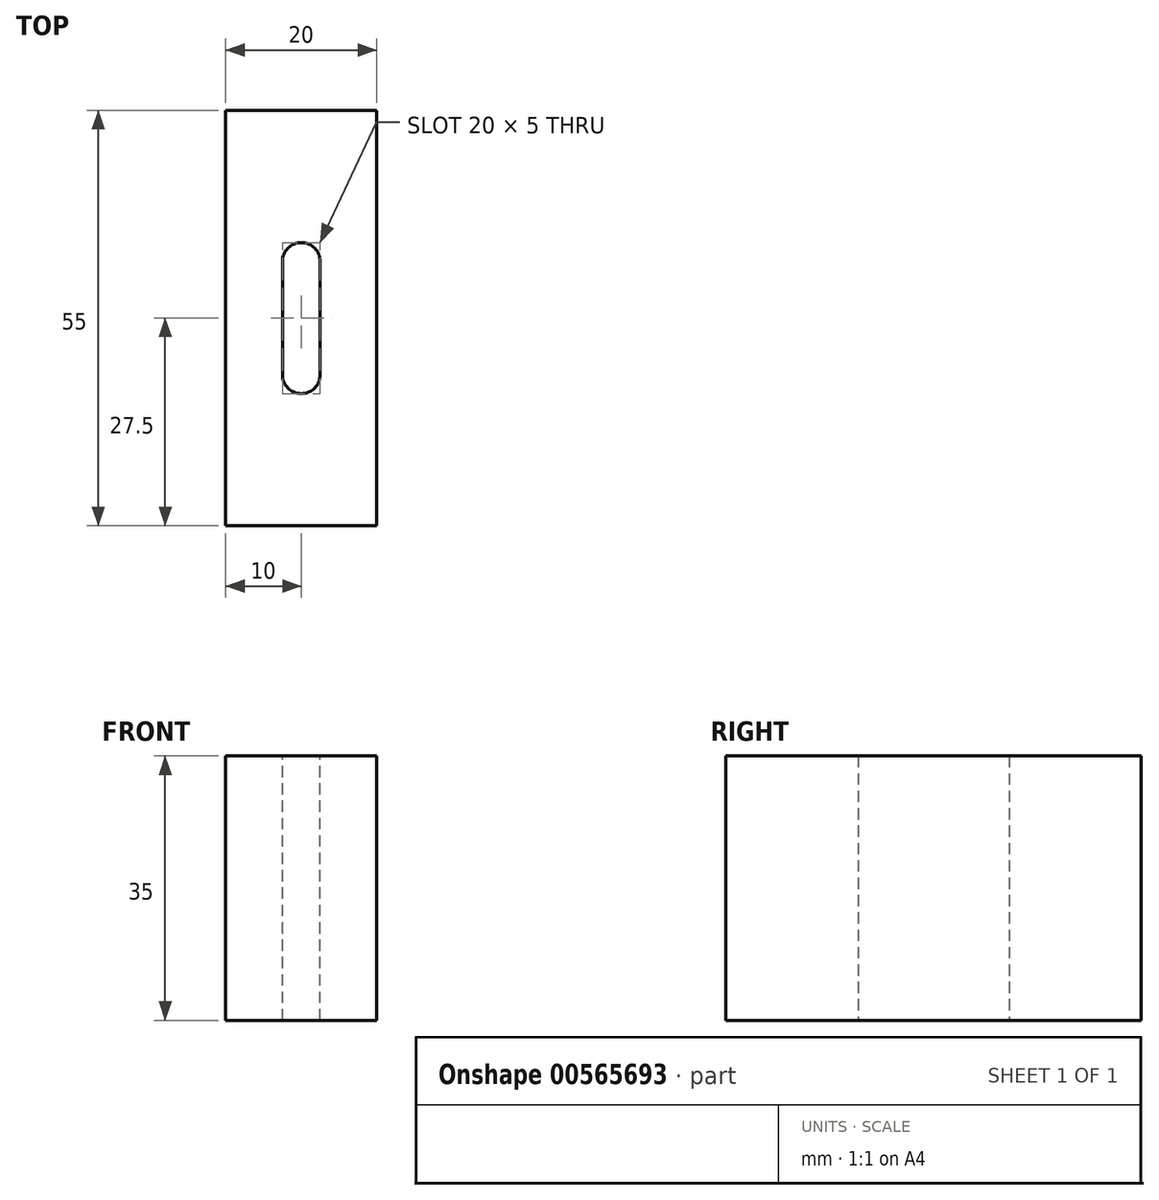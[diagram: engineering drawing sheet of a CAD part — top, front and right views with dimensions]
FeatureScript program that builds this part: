
annotation { "Feature Type Name" : "Feature", "Feature Type Description" : "" }
export const myFeature = defineFeature(function(context is Context, id is Id, definition is map)
    precondition{}
    {
        {
            var Q0;
            Q0=qCreatedBy(makeId("Top.planeOp"),FACE);
            var sketch = newSketch(context, id + "F0", { "sketchPlane" : qUnion([Q0])});
            skLineSegment(sketch, "E0.bottom", {"start": v(-10, -27.5) * mm, "end": v(10, -27.5) * mm});
            skLineSegment(sketch, "E0.top", {"start": v(-10, 27.5) * mm, "end": v(10, 27.5) * mm});
            skLineSegment(sketch, "E0.left", {"start": v(-10, -27.5) * mm, "end": v(-10, 27.5) * mm});
            skLineSegment(sketch, "E0.right", {"start": v(10, -27.5) * mm, "end": v(10, 27.5) * mm});
            skPoint(sketch, "E0.middle", {"position": v(0, 0) * mm});
            skSolve(sketch);
        }
        {
            var Q0;
            Q0 = qSketchRegion(id + "F0", true);
            extrude(context, id + "F1", {"entities" : qUnion([Q0]), "depth" : 35 * mm, "offsetDistance" : 25 * mm});
        }
        {
            var Q0;
            Q0=makeQuery(id+"F1.opExtrude","CAP_FACE",FACE,{"disambiguationData":[OSD([sQuery(id+"F0.wireOp",EDGE,"E0.bottom"),sQuery(id+"F0.wireOp",EDGE,"E0.top"),sQuery(id+"F0.wireOp",EDGE,"E0.left"),sQuery(id+"F0.wireOp",EDGE,"E0.right")])],"isStart":false});
            var sketch = newSketch(context, id + "F2", { "sketchPlane" : qUnion([Q0])});
            skLineSegment(sketch, "E1.bottom", {"start": v(-2.5, -10) * mm, "end": v(2.5, -10) * mm});
            skLineSegment(sketch, "E1.top", {"start": v(-2.5, 10) * mm, "end": v(2.5, 10) * mm});
            skLineSegment(sketch, "E1.left", {"start": v(-2.5, -10) * mm, "end": v(-2.5, 10) * mm});
            skLineSegment(sketch, "E1.right", {"start": v(2.5, -10) * mm, "end": v(2.5, 10) * mm});
            skPoint(sketch, "E1.middle", {"position": v(0, 0) * mm});
            skSolve(sketch);
        }
        {
            var Q0;
            Q0 = qSketchRegion(id + "F2", true);
            extrude(context, id + "F3", {"entities" : qUnion([Q0]), "operationType" : NewBodyOperationType.REMOVE, "endBound" : BoundingType.THROUGH_ALL, "oppositeDirection" : true, "depth" : 25 * mm, "offsetDistance" : 25 * mm});
        }
        {
            var Q0;
            Q0=makeQuery(id+"F3.boolean.opBoolean","COPY",EDGE,{"derivedFrom":makeQuery(id+"F3.opExtrude","SWEPT_EDGE",EDGE,{"disambiguationData":[OSD([sQuery(id+"F2.wireOp",EDGE,"E1.top"),sQuery(id+"F2.wireOp",EDGE,"E1.left")])]})});
            var Q1;
            Q1=makeQuery(id+"F3.boolean.opBoolean","COPY",EDGE,{"derivedFrom":makeQuery(id+"F3.opExtrude","SWEPT_EDGE",EDGE,{"disambiguationData":[OSD([sQuery(id+"F2.wireOp",EDGE,"E1.top"),sQuery(id+"F2.wireOp",EDGE,"E1.right")])]})});
            var Q2;
            Q2=makeQuery(id+"F3.boolean.opBoolean","COPY",EDGE,{"derivedFrom":makeQuery(id+"F3.opExtrude","SWEPT_EDGE",EDGE,{"disambiguationData":[OSD([sQuery(id+"F2.wireOp",EDGE,"E1.bottom"),sQuery(id+"F2.wireOp",EDGE,"E1.right")])]})});
            var Q3;
            Q3=makeQuery(id+"F3.boolean.opBoolean","COPY",EDGE,{"derivedFrom":makeQuery(id+"F3.opExtrude","SWEPT_EDGE",EDGE,{"disambiguationData":[OSD([sQuery(id+"F2.wireOp",EDGE,"E1.bottom"),sQuery(id+"F2.wireOp",EDGE,"E1.left")])]})});
            fillet(context, id + "F4", {"entities" : qUnion([Q0, Q1, Q2, Q3]), "radius" : 2.5 * mm, "tangentPropagation" : true, "allowEdgeOverflow" : false});
        }
    });
